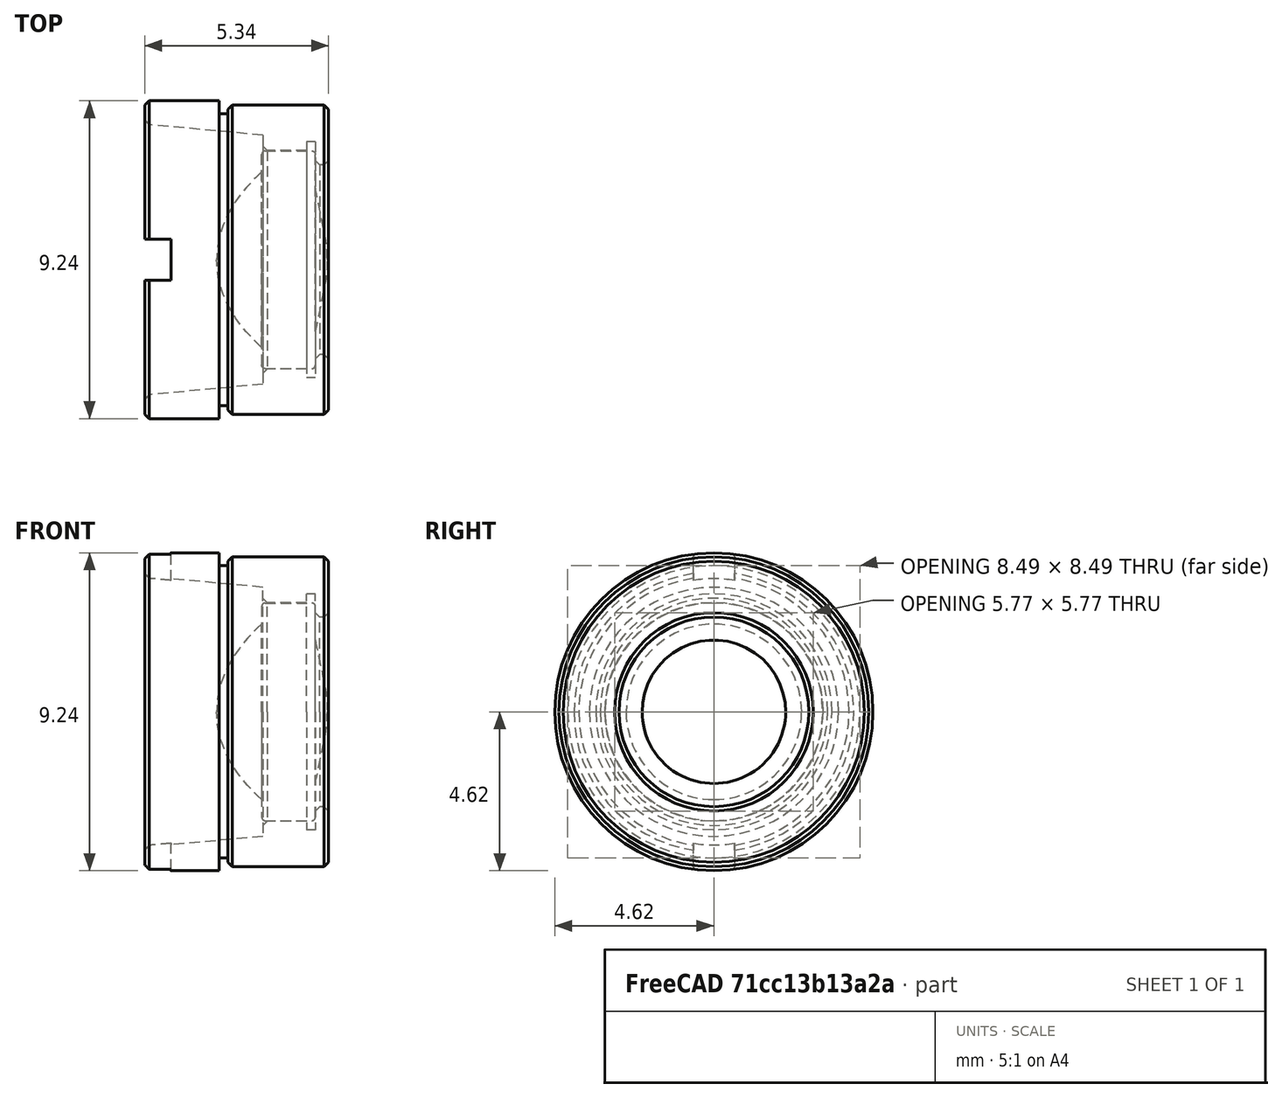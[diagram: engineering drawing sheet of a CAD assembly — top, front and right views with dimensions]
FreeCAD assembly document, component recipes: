
FREECAD ASSEMBLY — COMPONENT RECIPES ("imported-stepfile-as-surface-source")

This assembly document has 4 components, labeled P0..P3 below (a component is one placed body or linked part). 0 of them carry a construction recipe — the FreeCAD feature program that regenerates the part from scratch, quoted from this document or its linked companion documents; the rest are supplied as boundary geometry only. No exploded tour is included for this assembly.
COMPONENT P0 — geometry summary ("TTN021329-E0W003"; no construction recipe available for this part):
  bounding box: 6.5 x 6.4 x 3.7 mm
  tessellated surface: 16,536 triangles
  volume: 64 mm^3 (42% of its bounding box)
COMPONENT P1 — geometry summary ("housing"; no construction recipe available for this part):
  bounding box: 9.2 x 9.2 x 5.3 mm
  tessellated surface: 11,070 triangles
  volume: 130 mm^3 (29% of its bounding box)
  symmetry: 2-fold rotationally symmetric about the x axis; mirror-symmetric across its y mid-plane, z mid-plane
COMPONENT P2 — geometry summary ("lens"; no construction recipe available for this part):
  bounding box: 6.4 x 6.2 x 4.5 mm
  tessellated surface: 16,536 triangles
  volume: 64 mm^3 (36% of its bounding box)
COMPONENT P3 — geometry summary ("TTN021329-E0W002"; no construction recipe available for this part):
  bounding box: 9.2 x 9.2 x 5.3 mm
  tessellated surface: 27,606 triangles
  volume: 194 mm^3 (43% of its bounding box)
  symmetry: 2-fold rotationally symmetric about the x axis; mirror-symmetric across its y mid-plane, z mid-plane
PROVENANCE & LICENSES
A FreeCAD (.FCStd) document from a public repository crawl; recipes are the document's own serialized feature recipes (and, for linked parts, companion documents' recipes).
License: lgpl-3.0.
